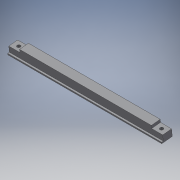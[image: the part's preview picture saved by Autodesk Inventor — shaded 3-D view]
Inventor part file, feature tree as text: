
AUTODESK INVENTOR PART (.ipt)
format: ipt  version: 2016 SP2 (Build 200236200, 236)  size: 136,192 bytes
history: native  units: mm
features: reference x9, extrude x4, sketch x3, mirror x1
ambient origin geometry x8: Origin, YZ Plane, XZ Plane, XY Plane, X Axis, Y Axis, Z Axis, Center Point
bodies: Volumenkörper1 (feature_tree)
feature tree (17):
  extrude  "Extrusion1"  Depth=10.0mm TaperAngle=0.0deg
  extrude  "Extrusion2"  Depth=3.1mm TaperAngle=0.0deg
  extrude  "Extrusion3"  Depth=3.4mm TaperAngle=0.0deg
  extrude  "Extrusion4"  [1 undecoded]
  mirror  "Spiegeln1"
  sketch  "Skizze2"  dims[d0=69.4mm d1=0.0mm d2=10.0mm d3=0.0mm]
  reference  "Referenz1"
  reference  "Referenz2"
  reference  "Referenz3"
  reference  "Referenz4"
  reference  "Referenz5"
  reference  "Referenz6"
  reference  "Referenz7"
  sketch  "Skizze3"  dims[d4=5.7mm d7=3.1mm d8=0.0mm]
  reference  "Referenz8"
  sketch  "Skizze5"  dims[d9=3.0mm d10=3.4mm d11=0.0mm]
  reference  "Referenz9"
note: 1 required parameter value undecoded (feature->parameter linkage not recoverable at this tier; creation-order binding heuristic only, values carry confidence <= 0.55)
